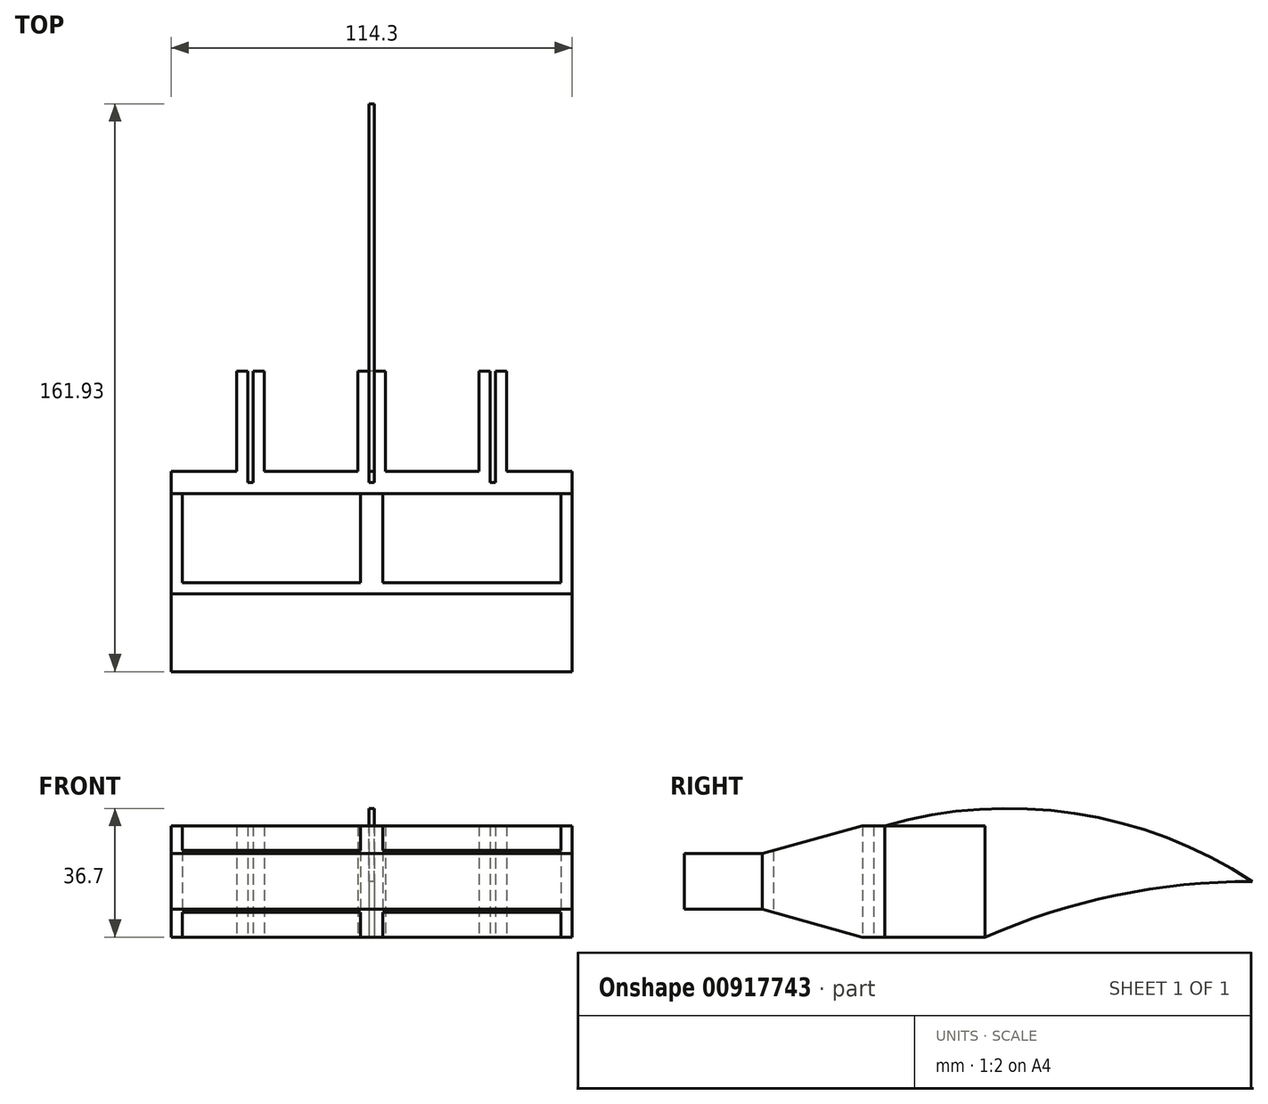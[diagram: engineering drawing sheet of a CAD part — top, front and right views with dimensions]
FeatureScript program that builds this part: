
annotation { "Feature Type Name" : "Feature", "Feature Type Description" : "" }
export const myFeature = defineFeature(function(context is Context, id is Id, definition is map)
    precondition{}
    {
        {
            var Q0;
            Q0=qCreatedBy(makeId("Top.planeOp"),FACE);
            var sketch = newSketch(context, id + "F0", { "sketchPlane" : qUnion([Q0])});
            skLineSegment(sketch, "E0.bottom", {"start": v(53.98, 0) * mm, "end": v(3.18, 0) * mm});
            skLineSegment(sketch, "E0.top", {"start": v(53.98, 25.4) * mm, "end": v(-53.98, 25.4) * mm});
            skLineSegment(sketch, "E0.left", {"start": v(53.98, 0) * mm, "end": v(53.98, 25.4) * mm});
            skLineSegment(sketch, "E0.right", {"start": v(-53.98, 0) * mm, "end": v(-53.98, 25.4) * mm});
            skPoint(sketch, "E0.middle", {"position": v(0, 12.7) * mm});
            skLineSegment(sketch, "E1.bottom", {"start": v(57.15, -3.17) * mm, "end": v(-57.15, -3.18) * mm});
            skLineSegment(sketch, "E1.top", {"start": v(57.15, 28.58) * mm, "end": v(-57.15, 28.58) * mm});
            skLineSegment(sketch, "E1.left", {"start": v(57.15, -3.17) * mm, "end": v(57.15, 28.58) * mm});
            skLineSegment(sketch, "E1.right", {"start": v(-57.15, -3.18) * mm, "end": v(-57.15, 28.58) * mm});
            skLineSegment(sketch, "E2", {"start": v(0, 0) * mm, "end": v(0, 25.4) * mm});
            skLineSegment(sketch, "E3", {"start": v(3.17, 25.4) * mm, "end": v(3.18, 0) * mm});
            skLineSegment(sketch, "E4", {"start": v(-3.18, 0) * mm, "end": v(-3.18, 25.4) * mm});
            skLineSegment(sketch, "E5.trimOffspring", {"start": v(-3.18, 0) * mm, "end": v(-53.98, 0) * mm});
            skLineSegment(sketch, "E6", {"start": v(0, 0) * mm, "end": v(0, -3.18) * mm});
            skLineSegment(sketch, "E7.bottom", {"start": v(-57.15, -3.18) * mm, "end": v(57.15, -3.18) * mm});
            skLineSegment(sketch, "E7.top", {"start": v(-57.15, -25.4) * mm, "end": v(57.15, -25.4) * mm});
            skLineSegment(sketch, "E7.left", {"start": v(-57.15, -3.18) * mm, "end": v(-57.15, -25.4) * mm});
            skLineSegment(sketch, "E7.right", {"start": v(57.15, -3.18) * mm, "end": v(57.15, -25.4) * mm});
            skLineSegment(sketch, "E8.bottom", {"start": v(0.8, 60.33) * mm, "end": v(3.97, 60.33) * mm});
            skLineSegment(sketch, "E8.top", {"start": v(0.8, 28.58) * mm, "end": v(32.54, 28.58) * mm});
            skLineSegment(sketch, "E8.left", {"start": v(0.8, 60.33) * mm, "end": v(0.8, 28.58) * mm});
            skLineSegment(sketch, "E9.bottom", {"start": v(-0.8, 60.33) * mm, "end": v(-3.97, 60.33) * mm});
            skLineSegment(sketch, "E9.top", {"start": v(-0.8, 28.58) * mm, "end": v(-32.54, 28.58) * mm});
            skLineSegment(sketch, "E9.left", {"start": v(-0.8, 60.33) * mm, "end": v(-0.8, 28.58) * mm});
            skLineSegment(sketch, "E10", {"start": v(3.97, 60.33) * mm, "end": v(3.97, 31.75) * mm});
            skLineSegment(sketch, "E11", {"start": v(-3.97, 31.75) * mm, "end": v(-3.97, 60.33) * mm});
            skLineSegment(sketch, "E12", {"start": v(-57.15, 31.75) * mm, "end": v(-57.15, 28.58) * mm});
            skLineSegment(sketch, "E13.MirrorCS", {"start": v(57.15, 31.75) * mm, "end": v(57.15, 28.58) * mm});
            skLineSegment(sketch, "E14", {"start": v(3.97, 31.75) * mm, "end": v(17.26, 31.75) * mm});
            skLineSegment(sketch, "E15", {"start": v(-3.97, 31.75) * mm, "end": v(-17.26, 31.75) * mm});
            skLineSegment(sketch, "E16.MirrorCS", {"start": v(-30.56, 31.75) * mm, "end": v(-30.56, 60.33) * mm});
            skLineSegment(sketch, "E17.MirrorCS", {"start": v(-33.73, 60.33) * mm, "end": v(-33.73, 28.58) * mm});
            skLineSegment(sketch, "E18.MirrorCS", {"start": v(-33.73, 60.33) * mm, "end": v(-30.56, 60.33) * mm});
            skLineSegment(sketch, "E19.MirrorCS", {"start": v(-35.32, 60.33) * mm, "end": v(-38.5, 60.33) * mm});
            skLineSegment(sketch, "E20.MirrorCS", {"start": v(-38.5, 60.33) * mm, "end": v(-38.5, 31.75) * mm});
            skLineSegment(sketch, "E21.MirrorCS", {"start": v(-35.32, 60.33) * mm, "end": v(-35.32, 28.58) * mm});
            skLineSegment(sketch, "E22.MirrorCS", {"start": v(33.73, 60.33) * mm, "end": v(33.73, 28.58) * mm});
            skLineSegment(sketch, "E23.MirrorCS", {"start": v(30.56, 60.33) * mm, "end": v(30.56, 31.75) * mm});
            skLineSegment(sketch, "E24.MirrorCS", {"start": v(33.73, 60.33) * mm, "end": v(30.56, 60.33) * mm});
            skLineSegment(sketch, "E25.MirrorCS", {"start": v(35.32, 60.33) * mm, "end": v(35.32, 28.58) * mm});
            skLineSegment(sketch, "E26.MirrorCS", {"start": v(38.5, 31.75) * mm, "end": v(38.5, 60.33) * mm});
            skLineSegment(sketch, "E27.MirrorCS", {"start": v(35.32, 60.33) * mm, "end": v(38.5, 60.33) * mm});
            skLineSegment(sketch, "E28", {"start": v(-57.15, 31.75) * mm, "end": v(-38.5, 31.75) * mm});
            skLineSegment(sketch, "E29", {"start": v(-30.56, 31.75) * mm, "end": v(-17.26, 31.75) * mm});
            skLineSegment(sketch, "E30", {"start": v(17.26, 31.75) * mm, "end": v(30.56, 31.75) * mm});
            skLineSegment(sketch, "E31", {"start": v(38.5, 31.75) * mm, "end": v(57.15, 31.75) * mm});
            skSolve(sketch);
        }
        {
            var Q0;
            Q0=makeQuery(id+"F0.imprint","IMPRINT",FACE,{"disambiguationData":[TD([[makeQuery(id+"F0.imprint","IMPRINT",EDGE,{"derivedFrom":sQuery(id+"F0.wireOp",EDGE,"E0.bottom")}),1.0]])]});
            var Q1;
            {var subQ0=sQuery(id+"F0.wireOp",EDGE,"E12");Q1=makeQuery(id+"F0.imprint","IMPRINT",FACE,{"disambiguationData":[TD([[makeQuery(id+"F0.imprint","IMPRINT",EDGE,{"derivedFrom":subQ0}),1.0]])]});}
            var Q2;
            {var subQ1=sQuery(id+"F0.wireOp",EDGE,"E13.MirrorCS");Q2=makeQuery(id+"F0.imprint","IMPRINT",FACE,{"disambiguationData":[TD([[makeQuery(id+"F0.imprint","IMPRINT",EDGE,{"derivedFrom":subQ1}),-1.0]])]});}
            var Q3;
            Q3=makeQuery(id+"F0.imprint","IMPRINT",FACE,{"disambiguationData":[TD([[makeQuery(id+"F0.imprint","IMPRINT",EDGE,{"derivedFrom":sQuery(id+"F0.wireOp",EDGE,"E8.bottom")}),-1.0]])]});
            var Q4;
            Q4=makeQuery(id+"F0.imprint","IMPRINT",FACE,{"disambiguationData":[TD([[makeQuery(id+"F0.imprint","IMPRINT",EDGE,{"derivedFrom":sQuery(id+"F0.wireOp",EDGE,"E9.bottom")}),1.0]])]});
            extrude(context, id + "F1", {"entities" : qUnion([Q0, Q1, Q2, Q3, Q4]), "depth" : 15.88 * mm, "offsetDistance" : 25.4 * mm, "hasSecondDirection" : true, "secondDirectionOppositeDirection" : true, "secondDirectionDepth" : 15.88 * mm});
        }
        {
            var Q0;
            Q0=makeQuery(id+"F0.imprint","IMPRINT",FACE,{"disambiguationData":[TD([[makeQuery(id+"F0.imprint","IMPRINT",EDGE,{"derivedFrom":sQuery(id+"F0.wireOp",EDGE,"E7.top")}),1.0]])]});
            extrude(context, id + "F2", {"entities" : qUnion([Q0]), "depth" : 7.95 * mm, "offsetDistance" : 25.4 * mm, "hasSecondDirection" : true, "secondDirectionOppositeDirection" : true, "secondDirectionDepth" : 7.95 * mm});
        }
        {
            var Q0;
            Q0=makeQuery(id+"F0.imprint","IMPRINT",FACE,{"disambiguationData":[TD([[makeQuery(id+"F0.imprint","IMPRINT",EDGE,{"derivedFrom":sQuery(id+"F0.wireOp",EDGE,"E9.bottom")}),1.0]])]});
            var Q1;
            Q1=makeQuery(id+"F0.imprint","IMPRINT",FACE,{"disambiguationData":[TD([[makeQuery(id+"F0.imprint","IMPRINT",EDGE,{"derivedFrom":sQuery(id+"F0.wireOp",EDGE,"E8.bottom")}),-1.0]])]});
            extrude(context, id + "F3", {"entities" : qUnion([Q0, Q1]), "operationType" : NewBodyOperationType.ADD, "depth" : 15.88 * mm, "offsetDistance" : 25.4 * mm, "hasSecondDirection" : true, "secondDirectionOppositeDirection" : true, "secondDirectionDepth" : 15.88 * mm});
        }
        {
            var Q0;
            Q0=sQuery(id+"F0.wireOp",EDGE,"E2");
            var Q1;
            Q1=sQuery(id+"F0.wireOp",EDGE,"E6");
            extrude(context, id + "F4", {"bodyType" : ToolBodyType.SURFACE, "surfaceEntities" : qUnion([Q0, Q1]), "depth" : 15.9 * mm, "offsetDistance" : 25.4 * mm, "hasSecondDirection" : true, "secondDirectionOppositeDirection" : true, "secondDirectionDepth" : 15.9 * mm});
        }
        {
            var Q0;
            Q0=makeQuery(id+"F4.opExtrude","SWEPT_BODY",BODY,{"disambiguationData":[OSD([sQuery(id+"F0.wireOp",EDGE,"E2"),sQuery(id+"F0.wireOp",EDGE,"E6")])]});
            deleteBodies(context, id + "F5", {"entities" : qUnion([Q0])});
        }
        {
            var Q0;
            Q0=qCreatedBy(makeId("Right.planeOp"),FACE);
            var sketch = newSketch(context, id + "F6", { "sketchPlane" : qUnion([Q0])});
            skLineSegment(sketch, "E32", {"start": v(-3.18, 7.95) * mm, "end": v(25.4, 15.9) * mm});
            skLineSegment(sketch, "E33", {"start": v(25.4, 15.9) * mm, "end": v(-3.18, 15.9) * mm});
            skLineSegment(sketch, "E34", {"start": v(-3.18, 15.9) * mm, "end": v(-3.17, 7.95) * mm});
            skLineSegment(sketch, "E35", {"start": v(-3.18, -7.95) * mm, "end": v(25.4, -15.9) * mm});
            skLineSegment(sketch, "E36", {"start": v(25.4, -15.9) * mm, "end": v(-3.18, -15.9) * mm});
            skLineSegment(sketch, "E37", {"start": v(-3.18, -15.9) * mm, "end": v(-3.18, -7.95) * mm});
            skSolve(sketch);
        }
        {
            var Q0;
            Q0=makeQuery(id+"F6.imprint","IMPRINT",FACE,{"disambiguationData":[TD([[makeQuery(id+"F6.imprint","IMPRINT",EDGE,{"derivedFrom":sQuery(id+"F6.wireOp",EDGE,"E35")}),-1.0]])]});
            var Q1;
            Q1=makeQuery(id+"F6.imprint","IMPRINT",FACE,{"disambiguationData":[TD([[makeQuery(id+"F6.imprint","IMPRINT",EDGE,{"derivedFrom":sQuery(id+"F6.wireOp",EDGE,"E32")}),1.0]])]});
            extrude(context, id + "F7", {"entities" : qUnion([Q0, Q1]), "operationType" : NewBodyOperationType.REMOVE, "oppositeDirection" : true, "depth" : 57.15 * mm, "offsetDistance" : 25.4 * mm, "hasSecondDirection" : true, "secondDirectionOppositeDirection" : false, "secondDirectionDepth" : 57.15 * mm});
        }
        {
            var Q0;
            Q0=qCreatedBy(makeId("Right.planeOp"),FACE);
            var sketch = newSketch(context, id + "F8", { "sketchPlane" : qUnion([Q0])});
            skPoint(sketch, "E38", {"position": v(31.75, 15.88) * mm});
            skPoint(sketch, "E39", {"position": v(31.75, -15.88) * mm});
            skPoint(sketch, "E40", {"position": v(60.33, -15.87) * mm});
            skPoint(sketch, "E41", {"position": v(60.33, 15.88) * mm});
            skArc(sketch, "E42", {"start": v(136.53, 0) * mm, "mid": v(85.87, 19.39) * mm, "end": v(31.75, 15.88) * mm});
            skArc(sketch, "E43", {"start": v(136.53, 0) * mm, "mid": v(97.6, -4.01) * mm, "end": v(60.33, -15.87) * mm});
            skLineSegment(sketch, "E44", {"start": v(-65.94, 0) * mm, "end": v(170.17, 0) * mm, "construction": true});
            skLineSegment(sketch, "E45", {"start": v(31.75, 15.88) * mm, "end": v(31.75, -15.88) * mm});
            skLineSegment(sketch, "E46", {"start": v(31.75, -15.88) * mm, "end": v(60.33, -15.88) * mm});
            skSolve(sketch);
        }
        {
            var Q0;
            Q0=makeQuery(id+"F8.imprint","IMPRINT",FACE,{"disambiguationData":[TD([[makeQuery(id+"F8.imprint","IMPRINT",EDGE,{"derivedFrom":sQuery(id+"F8.wireOp",EDGE,"E42")}),1.0]])]});
            extrude(context, id + "F9", {"entities" : qUnion([Q0]), "depth" : 0.8 * mm, "offsetDistance" : 25.4 * mm, "hasSecondDirection" : true, "secondDirectionOppositeDirection" : true, "secondDirectionDepth" : 0.8 * mm});
        }
    });
